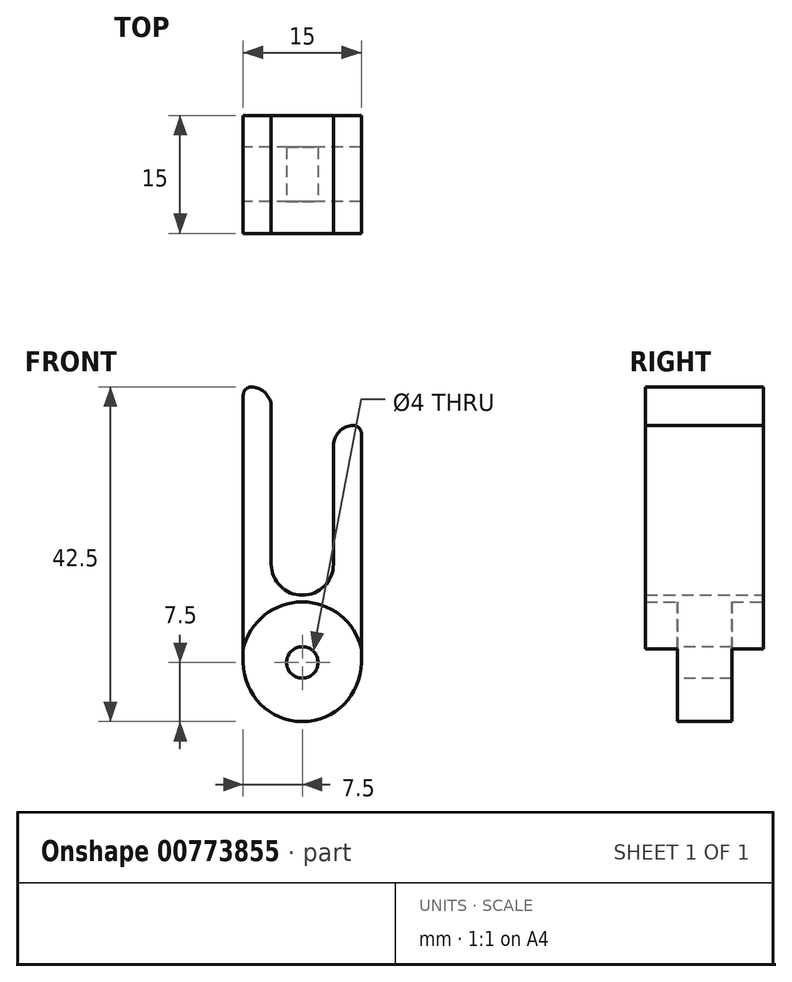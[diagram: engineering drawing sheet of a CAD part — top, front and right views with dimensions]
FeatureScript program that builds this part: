
annotation { "Feature Type Name" : "Feature", "Feature Type Description" : "" }
export const myFeature = defineFeature(function(context is Context, id is Id, definition is map)
    precondition{}
    {
        {
            var Q0;
            Q0=qCreatedBy(makeId("Front.planeOp"),FACE);
            var sketch = newSketch(context, id + "F0", { "sketchPlane" : qUnion([Q0])});
            skLineSegment(sketch, "E0", {"start": v(-7.5, 0) * mm, "end": v(-7.5, 34) * mm});
            skArc(sketch, "E1", {"start": v(-3.95, 12.5) * mm, "mid": v(0, 8.55) * mm, "end": v(3.95, 12.5) * mm});
            skArc(sketch, "E2", {"start": v(-6.5, 35) * mm, "mid": v(-7.2, 34.7) * mm, "end": v(-7.5, 34) * mm});
            skArc(sketch, "E3", {"start": v(-3.95, 32.45) * mm, "mid": v(-4.7, 34.25) * mm, "end": v(-6.5, 35) * mm});
            skLineSegment(sketch, "E4", {"start": v(-3.95, 32.45) * mm, "end": v(-3.95, 12.5) * mm});
            skArc(sketch, "E5", {"start": v(7.5, 29.1) * mm, "mid": v(7.2, 29.8) * mm, "end": v(6.5, 30.1) * mm});
            skArc(sketch, "E6", {"start": v(6.5, 30.1) * mm, "mid": v(4.7, 29.35) * mm, "end": v(3.95, 27.55) * mm});
            skLineSegment(sketch, "E7", {"start": v(3.95, 27.55) * mm, "end": v(3.95, 12.5) * mm});
            skLineSegment(sketch, "E8", {"start": v(7.5, 29.1) * mm, "end": v(7.5, 0) * mm});
            skArc(sketch, "E9", {"start": v(-7.5, 0) * mm, "mid": v(0, -7.5) * mm, "end": v(7.5, 0) * mm});
            skLineSegment(sketch, "E10", {"start": v(0, 0) * mm, "end": v(0, 7.7) * mm});
            skLineSegment(sketch, "E11", {"start": v(0, 0) * mm, "end": v(-7.5, 0) * mm});
            skLineSegment(sketch, "E12", {"start": v(0, 0) * mm, "end": v(7.5, 0) * mm});
            skArc(sketch, "E13", {"start": v(7.5, 1.75) * mm, "mid": v(0, 7.7) * mm, "end": v(-7.5, 1.74) * mm});
            skSolve(sketch);
        }
        {
            var Q0;
            Q0=makeQuery(id+"F0.imprint","IMPRINT",FACE,{"disambiguationData":[TD([[makeQuery(id+"F0.imprint","IMPRINT",EDGE,{"derivedFrom":sQuery(id+"F0.wireOp",EDGE,"E1")}),-1.0]])]});
            extrude(context, id + "F1", {"entities" : qUnion([Q0]), "endBound" : BoundingType.SYMMETRIC, "depth" : 15 * mm, "offsetDistance" : 25 * mm});
        }
        {
            var Q0;
            Q0=makeQuery(id+"F0.imprint","IMPRINT",FACE,{"disambiguationData":[TD([[makeQuery(id+"F0.imprint","IMPRINT",EDGE,{"derivedFrom":sQuery(id+"F0.wireOp",EDGE,"E9")}),1.0]])]});
            var Q1;
            {var subQ4=sQuery(id+"F0.wireOp",EDGE,"E10");Q1=makeQuery(id+"F0.imprint","IMPRINT",FACE,{"disambiguationData":[TD([[makeQuery(id+"F0.imprint","IMPRINT",EDGE,{"derivedFrom":subQ4}),1.0]])]});}
            var Q2;
            {var subQ4=sQuery(id+"F0.wireOp",EDGE,"E10");Q2=makeQuery(id+"F0.imprint","IMPRINT",FACE,{"disambiguationData":[TD([[makeQuery(id+"F0.imprint","IMPRINT",EDGE,{"derivedFrom":subQ4}),-1.0]])]});}
            extrude(context, id + "F2", {"entities" : qUnion([Q0, Q1, Q2]), "operationType" : NewBodyOperationType.ADD, "endBound" : BoundingType.SYMMETRIC, "depth" : 6.9 * mm, "offsetDistance" : 25 * mm});
        }
        {
            var Q0;
            Q0=makeQuery(id+"F2.opExtrude","CAP_FACE",FACE,{"disambiguationData":[OSD([sQuery(id+"F0.wireOp",EDGE,"E0"),sQuery(id+"F0.wireOp",EDGE,"E8"),sQuery(id+"F0.wireOp",EDGE,"E9"),sQuery(id+"F0.wireOp",EDGE,"E13")])],"isStart":false});
            var sketch = newSketch(context, id + "F3", { "sketchPlane" : qUnion([Q0])});
            skPoint(sketch, "E14", {"position": v(0, 0) * mm});
            skSolve(sketch);
        }
        {
            var Q0;
            Q0=sQuery(id+"F3.wireOp",VERTEX,"E14");
            var Q1;
            Q1=makeQuery(id+"F1.opExtrude","SWEPT_BODY",BODY,{"disambiguationData":[OSD([sQuery(id+"F0.wireOp",EDGE,"E0"),sQuery(id+"F0.wireOp",EDGE,"E1"),sQuery(id+"F0.wireOp",EDGE,"E2"),sQuery(id+"F0.wireOp",EDGE,"E3"),sQuery(id+"F0.wireOp",EDGE,"E4"),sQuery(id+"F0.wireOp",EDGE,"E5"),sQuery(id+"F0.wireOp",EDGE,"E6"),sQuery(id+"F0.wireOp",EDGE,"E7"),sQuery(id+"F0.wireOp",EDGE,"E8"),sQuery(id+"F0.wireOp",EDGE,"E13")])]});
            hole(context, id + "F4", {"style" : HoleStyle.SIMPLE, "endStyle" : HoleEndStyle.THROUGH, "holeDiameter" : 4 * mm, "majorDiameter" : 5 * mm, "isTappedThrough" : true, "tappedDepth" : 12 * mm, "tapClearance" : 3, "locations" : qUnion([Q0]), "scope" : qUnion([Q1])});
        }
    });
